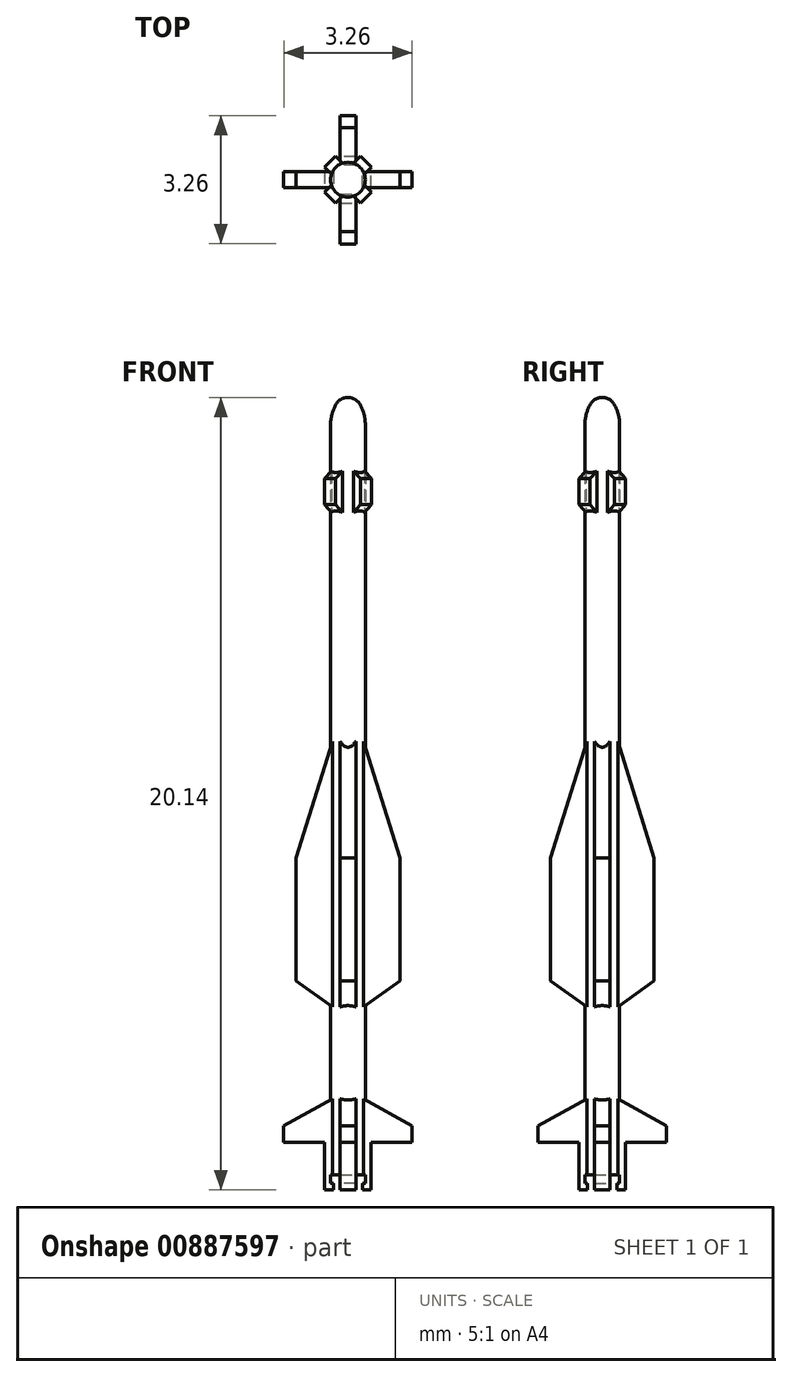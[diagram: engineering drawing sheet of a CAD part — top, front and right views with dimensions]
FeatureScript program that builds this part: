
annotation { "Feature Type Name" : "Feature", "Feature Type Description" : "" }
export const myFeature = defineFeature(function(context is Context, id is Id, definition is map)
    precondition{}
    {
        {
            var Q0;
            Q0=qCreatedBy(makeId("Front.planeOp"),FACE);
            var sketch = newSketch(context, id + "F0", { "sketchPlane" : qUnion([Q0])});
            skLineSegment(sketch, "E0", {"start": v(0, 0) * mm, "end": v(0, 19.76) * mm});
            skLineSegment(sketch, "E1", {"start": v(0.44, 19.06) * mm, "end": v(0.44, 0) * mm});
            skLineSegment(sketch, "E2", {"start": v(0.44, 0) * mm, "end": v(0, 0) * mm});
            skArc(sketch, "E3", {"start": v(0.3, 19.58) * mm, "mid": v(0.17, 19.71) * mm, "end": v(0, 19.76) * mm});
            skArc(sketch, "E4", {"start": v(0.44, 19.06) * mm, "mid": v(0.4, 19.33) * mm, "end": v(0.3, 19.58) * mm});
            skSolve(sketch);
        }
        {
            var Q0;
            {var subQ0=sQuery(id+"F0.wireOp",EDGE,"mrwio9nY-PsAZ-Zbfy-NhIU-sYq0QVbgGXAG");Q0=makeQuery(id+"F0.imprint","IMPRINT",FACE,{"disambiguationData":[TD([[makeQuery(id+"F0.imprint","IMPRINT",EDGE,{"derivedFrom":subQ0}),-1.0]])]});}
            var Q1;
            Q1=makeQuery(id+"F0.imprint","IMPRINT",FACE,{"disambiguationData":[TD([[makeQuery(id+"F0.imprint","IMPRINT",EDGE,{"derivedFrom":sQuery(id+"F0.wireOp",EDGE,"rEedh4zr-IGRr-Hqzj-sDLB-QnI7VE1V64O6.bottom")}),-1.0]])]});
            var Q2;
            Q2=makeQuery(id+"F0.imprint","IMPRINT",FACE,{"disambiguationData":[TD([[makeQuery(id+"F0.imprint","IMPRINT",EDGE,{"derivedFrom":sQuery(id+"F0.wireOp",EDGE,"E0")}),-1.0]])]});
            var Q3;
            Q3=makeQuery(id+"F0.imprint","IMPRINT",FACE,{"disambiguationData":[TD([[makeQuery(id+"F0.imprint","IMPRINT",EDGE,{"derivedFrom":sQuery(id+"F0.wireOp",EDGE,"p5wuz8j9-3HT4-kWwn-DjtP-lJmqTNSXSBJY.bottom")}),-1.0]])]});
            var Q4;
            Q4=sQuery(id+"F0.wireOp",EDGE,"E0");
            revolve(context, id + "F1", {"surfaceOperationType" : NewSurfaceOperationType.NEW, "entities" : qUnion([Q0, Q1, Q2, Q3]), "axis" : qUnion([Q4]), "revolveType" : RevolveType.FULL});
        }
        {
            var Q0;
            Q0=qCreatedBy(makeId("Front.planeOp"),FACE);
            var sketch = newSketch(context, id + "F2", { "sketchPlane" : qUnion([Q0])});
            skLineSegment(sketch, "E5", {"start": v(0, 0) * mm, "end": v(0, 16.56) * mm});
            skLineSegment(sketch, "E6", {"start": v(0.44, -0.2) * mm, "end": v(0.44, 32.87) * mm, "construction": true});
            skLineSegment(sketch, "E7", {"start": v(0.6, -0.38) * mm, "end": v(0.37, -0.38) * mm});
            skLineSegment(sketch, "E8", {"start": v(0.6, -0.38) * mm, "end": v(0.6, 0.83) * mm});
            skLineSegment(sketch, "E9", {"start": v(0.6, 0.83) * mm, "end": v(1.63, 0.83) * mm});
            skLineSegment(sketch, "E10.0", {"start": v(0.44, 0) * mm, "end": v(-0.44, 0) * mm});
            skLineSegment(sketch, "E11", {"start": v(1.63, 0.83) * mm, "end": v(1.63, 1.25) * mm});
            skLineSegment(sketch, "E12", {"start": v(1.63, 1.25) * mm, "end": v(0, 2.15) * mm});
            skLineSegment(sketch, "E13", {"start": v(0.44, -0.2) * mm, "end": v(0.44, 0) * mm});
            skPoint(sketch, "E14", {"position": v(0.44, 1.9) * mm});
            skLineSegment(sketch, "E15", {"start": v(0.37, -0.38) * mm, "end": v(0.37, -0.2) * mm});
            skLineSegment(sketch, "E16", {"start": v(0.37, -0.2) * mm, "end": v(0.44, -0.2) * mm});
            skLineSegment(sketch, "E17", {"start": v(0, 4) * mm, "end": v(1.32, 4.93) * mm});
            skLineSegment(sketch, "E18", {"start": v(1.32, 4.93) * mm, "end": v(1.32, 8.06) * mm});
            skLineSegment(sketch, "E19", {"start": v(1.32, 8.06) * mm, "end": v(0, 12.28) * mm});
            skPoint(sketch, "E20", {"position": v(0.44, 10.87) * mm});
            skPoint(sketch, "E21", {"position": v(0.44, 4.3) * mm});
            skSolve(sketch);
        }
        {
            var Q0;
            Q0=qSketchRegion(id+"F2",true);
            extrude(context, id + "F3", {"entities" : qUnion([Q0]), "operationType" : NewBodyOperationType.ADD, "depth" : .4 * mm, "offsetDistance" : 25 * mm, "symmetric" : true});
        }
        {
            var Q0;
            Q0=qCreatedBy(makeId("Front.planeOp"),FACE);
            var Q1;
            Q1=qCreatedBy(makeId("Right.planeOp"),FACE);
            cPlane(context, id + "F4", {"entities" : qUnion([Q0, Q1]), "cplaneType" : CPlaneType.MID_PLANE, "offset" : 25 * mm, "width" : 150 * mm, "height" : 150 * mm});
        }
        {
            var Q0;
            Q0=qCreatedBy(id+"F4.planeOp",FACE);
            var sketch = newSketch(context, id + "F5", { "sketchPlane" : qUnion([Q0])});
            skLineSegment(sketch, "E22", {"start": v(0.64, 17.03) * mm, "end": v(0.64, 17.7) * mm});
            skLineSegment(sketch, "E23", {"start": v(0, 19.9) * mm, "end": v(0, 14.41) * mm});
            skLineSegment(sketch, "E24.0", {"start": v(0.44, 19.06) * mm, "end": v(-0.44, 19.06) * mm});
            skLineSegment(sketch, "E25", {"start": v(0.44, 19.06) * mm, "end": v(0.44, 14.07) * mm, "construction": true});
            skLineSegment(sketch, "E26", {"start": v(0.64, 17.7) * mm, "end": v(0, 18.19) * mm});
            skLineSegment(sketch, "E27", {"start": v(0.64, 17.03) * mm, "end": v(0, 16.53) * mm});
            skPoint(sketch, "E28", {"position": v(0.44, 17.85) * mm});
            skPoint(sketch, "E29", {"position": v(0.44, 16.88) * mm});
            skSolve(sketch);
        }
        {
            var Q0;
            Q0=qSketchRegion(id+"F5",true);
            extrude(context, id + "F6", {"entities" : qUnion([Q0]), "operationType" : NewBodyOperationType.ADD, "depth" : .4 * mm, "offsetDistance" : 25 * mm, "symmetric" : true});
        }
        {
            var Q0;
            Q0=makeQuery(id+"F1.opRevolve","SWEPT_BODY",BODY,{"disambiguationData":[OSD([sQuery(id+"F0.wireOp",EDGE,"E0"),sQuery(id+"F0.wireOp",EDGE,"E1"),sQuery(id+"F0.wireOp",EDGE,"E2"),sQuery(id+"F0.wireOp",EDGE,"2EiOItwe-9FNA-eY8p-DkXH-AMy5AHyUmzZA"),sQuery(id+"F0.wireOp",EDGE,"lF35QjYl-MEgV-fRWE-0Yr6-Bt5vS8A7brRf")])]});
            var Q1;
            Q1=makeQuery(id+"F1.opRevolve","SWEPT_FACE",FACE,{"disambiguationData":[OSD([sQuery(id+"F0.wireOp",EDGE,"E1")])]});
            circularPattern(context, id + "F7", {"operationType" : NewBodyOperationType.ADD, "entities" : qUnion([Q0]), "axis" : qUnion([Q1]), "angle" : 360 * degree, "instanceCount" : 4, "equalSpace" : true, "computeTransformsWithoutBuiltin" : true});
        }
    });
